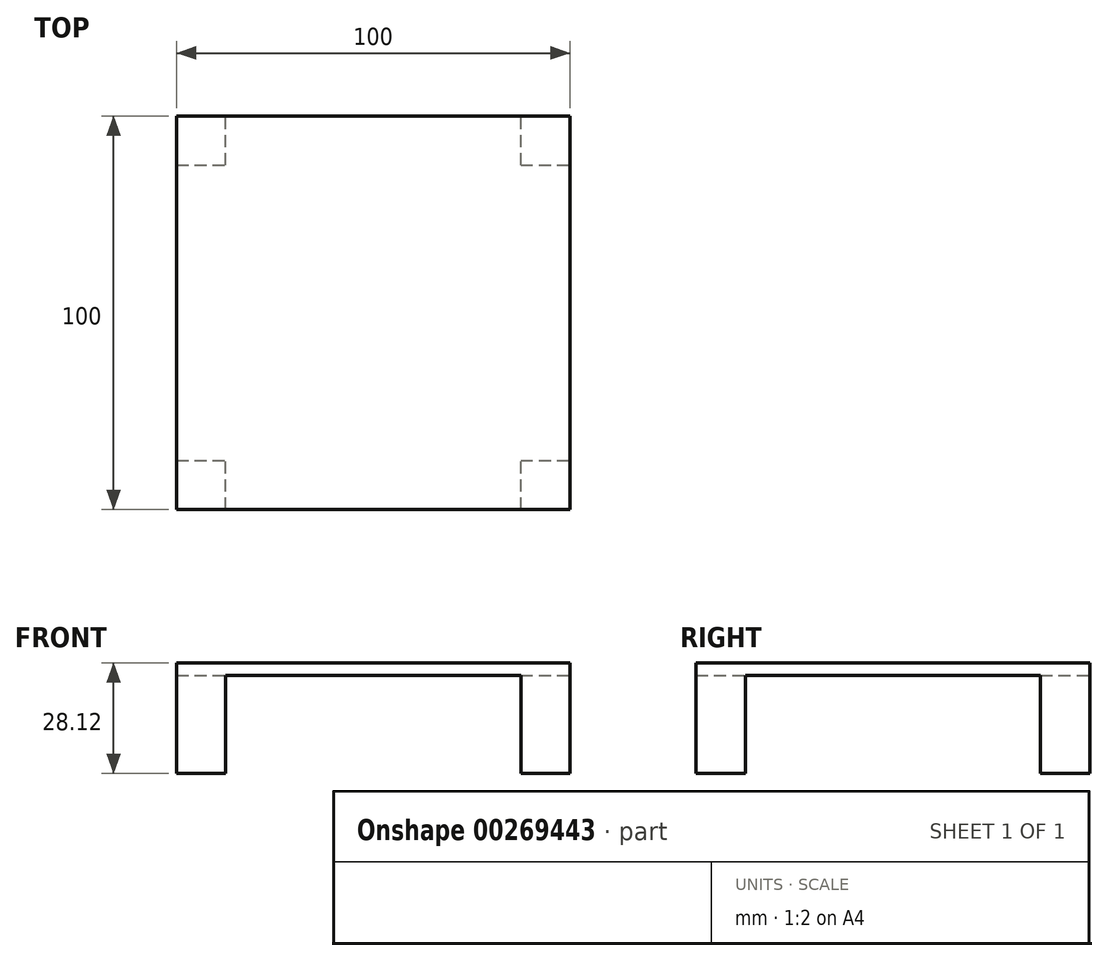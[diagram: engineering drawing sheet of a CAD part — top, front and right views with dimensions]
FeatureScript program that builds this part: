
annotation { "Feature Type Name" : "Feature", "Feature Type Description" : "" }
export const myFeature = defineFeature(function(context is Context, id is Id, definition is map)
    precondition{}
    {
        {
            var Q0;
            Q0=qCreatedBy(makeId("Top.planeOp"),FACE);
            var sketch = newSketch(context, id + "F0", { "sketchPlane" : qUnion([Q0])});
            skLineSegment(sketch, "E0.bottom", {"start": v(-72.35, -36.85) * mm, "end": v(27.65, -36.85) * mm});
            skLineSegment(sketch, "E0.top", {"start": v(-72.35, 63.15) * mm, "end": v(27.65, 63.15) * mm});
            skLineSegment(sketch, "E0.left", {"start": v(-72.35, -36.85) * mm, "end": v(-72.35, 63.15) * mm});
            skLineSegment(sketch, "E0.right", {"start": v(27.65, -36.85) * mm, "end": v(27.65, 63.15) * mm});
            skSolve(sketch);
        }
        {
            var Q0;
            Q0 = qSketchRegion(id + "F0", true);
            extrude(context, id + "F1", {"entities" : qUnion([Q0]), "depth" : 3.12 * mm});
        }
        {
            var Q0;
            Q0=qCreatedBy(makeId("Top.planeOp"),FACE);
            var sketch = newSketch(context, id + "F2", { "sketchPlane" : qUnion([Q0])});
            skLineSegment(sketch, "E1.bottom", {"start": v(-72.35, -36.85) * mm, "end": v(-59.85, -36.85) * mm});
            skLineSegment(sketch, "E1.top", {"start": v(-72.35, -24.35) * mm, "end": v(-59.85, -24.35) * mm});
            skLineSegment(sketch, "E1.left", {"start": v(-72.35, -36.85) * mm, "end": v(-72.35, -24.35) * mm});
            skLineSegment(sketch, "E1.right", {"start": v(-59.85, -36.85) * mm, "end": v(-59.85, -24.35) * mm});
            skLineSegment(sketch, "E2.bottom", {"start": v(15.15, -36.85) * mm, "end": v(27.65, -36.85) * mm});
            skLineSegment(sketch, "E2.top", {"start": v(15.15, -24.35) * mm, "end": v(27.65, -24.35) * mm});
            skLineSegment(sketch, "E2.left", {"start": v(15.15, -36.85) * mm, "end": v(15.15, -24.35) * mm});
            skLineSegment(sketch, "E2.right", {"start": v(27.65, -36.85) * mm, "end": v(27.65, -24.35) * mm});
            skLineSegment(sketch, "E3.bottom", {"start": v(-72.35, 50.65) * mm, "end": v(-59.85, 50.65) * mm});
            skLineSegment(sketch, "E3.top", {"start": v(-72.35, 63.15) * mm, "end": v(-59.85, 63.15) * mm});
            skLineSegment(sketch, "E3.left", {"start": v(-72.35, 50.65) * mm, "end": v(-72.35, 63.15) * mm});
            skLineSegment(sketch, "E3.right", {"start": v(-59.85, 50.65) * mm, "end": v(-59.85, 63.15) * mm});
            skLineSegment(sketch, "E4.bottom", {"start": v(15.15, 50.65) * mm, "end": v(27.65, 50.65) * mm});
            skLineSegment(sketch, "E4.top", {"start": v(15.15, 63.15) * mm, "end": v(27.65, 63.15) * mm});
            skLineSegment(sketch, "E4.left", {"start": v(15.15, 50.65) * mm, "end": v(15.15, 63.15) * mm});
            skLineSegment(sketch, "E4.right", {"start": v(27.65, 50.65) * mm, "end": v(27.65, 63.15) * mm});
            skSolve(sketch);
        }
        {
            var Q0;
            Q0 = qSketchRegion(id + "F2", true);
            extrude(context, id + "F3", {"entities" : qUnion([Q0]), "operationType" : NewBodyOperationType.ADD, "oppositeDirection" : true, "depth" : 25 * mm});
        }
    });
